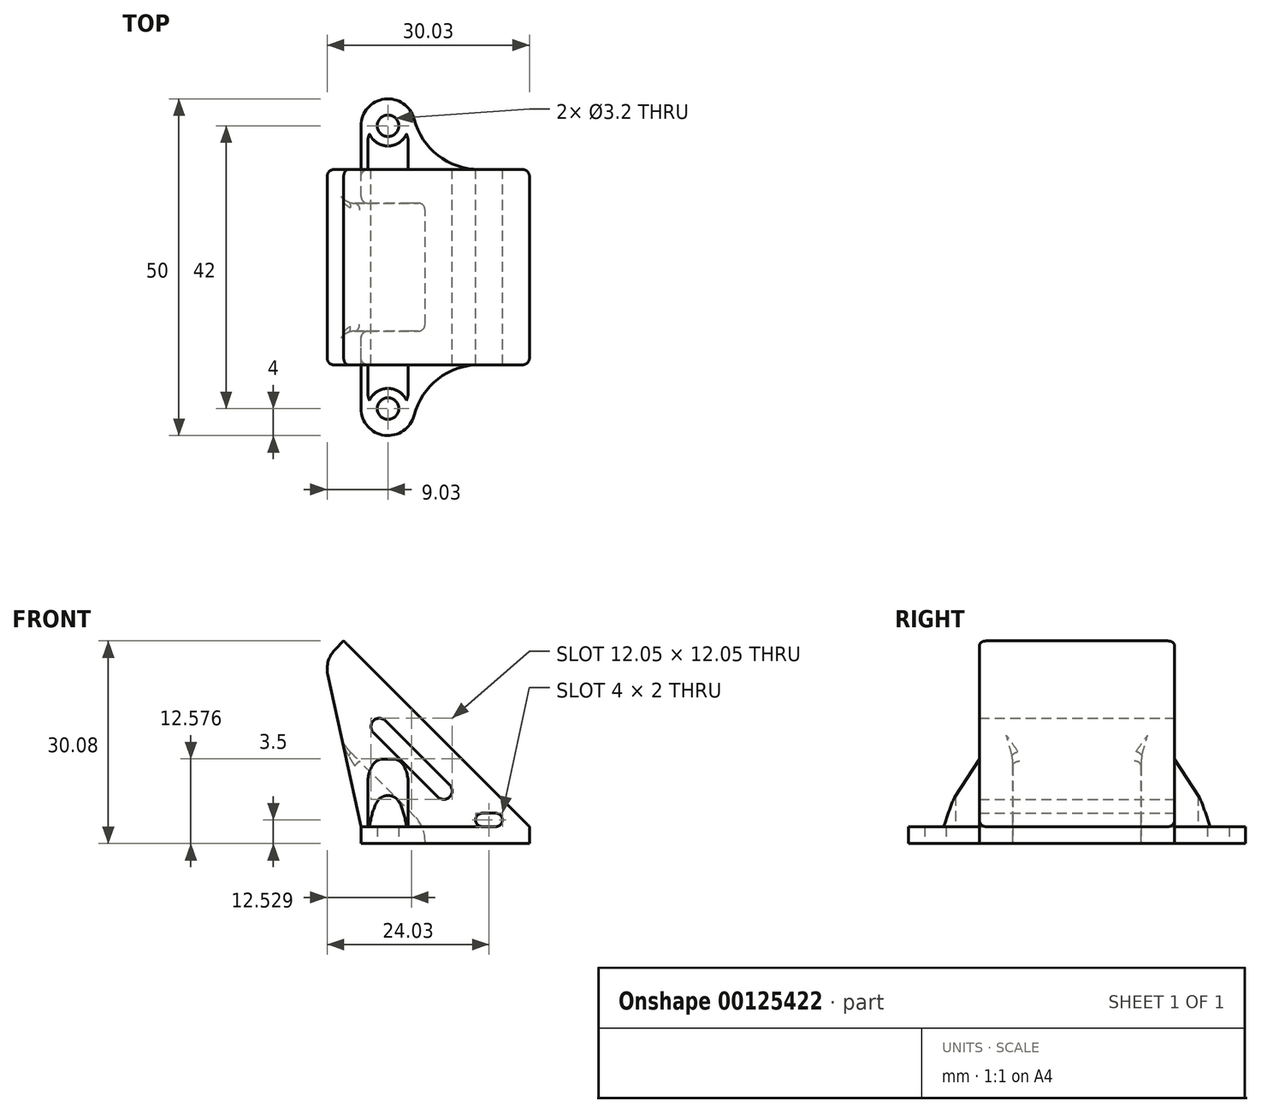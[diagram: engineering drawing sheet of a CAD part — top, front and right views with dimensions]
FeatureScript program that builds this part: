
annotation { "Feature Type Name" : "Feature", "Feature Type Description" : "" }
export const myFeature = defineFeature(function(context is Context, id is Id, definition is map)
    precondition{}
    {
        {
            var Q0;
            Q0=qCreatedBy(makeId("Front.planeOp"),FACE);
            var sketch = newSketch(context, id + "F0", { "sketchPlane" : qUnion([Q0])});
            skLineSegment(sketch, "E0", {"start": v(-27.58, 30.08) * mm, "end": v(0, 2.5) * mm});
            skLineSegment(sketch, "E1", {"start": v(-27.58, 30.08) * mm, "end": v(-28.86, 28.8) * mm});
            skLineSegment(sketch, "E2", {"start": v(-29.94, 25.11) * mm, "end": v(-25, 2.5) * mm});
            skLineSegment(sketch, "E3", {"start": v(0, 0) * mm, "end": v(0, 2.5) * mm});
            skLineSegment(sketch, "E4", {"start": v(-23.16, 18.23) * mm, "end": v(-23.16, 18.23) * mm});
            skLineSegment(sketch, "E5", {"start": v(-23.16, 16.47) * mm, "end": v(-13.61, 6.92) * mm});
            skLineSegment(sketch, "E6", {"start": v(-11.84, 6.92) * mm, "end": v(-11.84, 6.92) * mm});
            skLineSegment(sketch, "E7", {"start": v(-11.84, 8.69) * mm, "end": v(-21.39, 18.23) * mm});
            skLineSegment(sketch, "E8", {"start": v(-13.79, 16.29) * mm, "end": v(-16.62, 13.46) * mm, "construction": true});
            skPoint(sketch, "E9.visualSharp", {"position": v(-22.27, 19.12) * mm});
            skArc(sketch, "E9.filletArc", {"start": v(-21.39, 18.23) * mm, "mid": v(-22.27, 18.6) * mm, "end": v(-23.16, 18.23) * mm});
            skPoint(sketch, "E10.visualSharp", {"position": v(-10.96, 7.8) * mm});
            skArc(sketch, "E10.filletArc", {"start": v(-11.84, 6.92) * mm, "mid": v(-11.48, 7.8) * mm, "end": v(-11.84, 8.69) * mm});
            skPoint(sketch, "E11.visualSharp", {"position": v(-12.73, 6.04) * mm});
            skArc(sketch, "E11.filletArc", {"start": v(-13.61, 6.92) * mm, "mid": v(-12.73, 6.55) * mm, "end": v(-11.84, 6.92) * mm});
            skPoint(sketch, "E12.visualSharp", {"position": v(-24.04, 17.35) * mm});
            skArc(sketch, "E12.filletArc", {"start": v(-23.16, 18.23) * mm, "mid": v(-23.52, 17.35) * mm, "end": v(-23.16, 16.47) * mm});
            skLineSegment(sketch, "E13", {"start": v(-7, 3.5) * mm, "end": v(-5, 3.5) * mm, "construction": true});
            skArc(sketch, "E14.0.startCap", {"start": v(-7, 2.5) * mm, "mid": v(-8, 3.5) * mm, "end": v(-7, 4.5) * mm});
            skArc(sketch, "E14.0.endCap", {"start": v(-5, 4.5) * mm, "mid": v(-4, 3.5) * mm, "end": v(-5, 2.5) * mm});
            skLineSegment(sketch, "E14.0.left", {"start": v(-7, 4.5) * mm, "end": v(-5, 4.5) * mm});
            skLineSegment(sketch, "E14.0.right", {"start": v(-7, 2.5) * mm, "end": v(-5, 2.5) * mm});
            skPoint(sketch, "E15.visualSharp", {"position": v(-30.4, 27.25) * mm});
            skArc(sketch, "E15.filletArc", {"start": v(-28.86, 28.8) * mm, "mid": v(-29.87, 27.1) * mm, "end": v(-29.94, 25.11) * mm});
            skLineSegment(sketch, "E16", {"start": v(0, 0) * mm, "end": v(-25, 0) * mm});
            skLineSegment(sketch, "E17", {"start": v(-25, 2.5) * mm, "end": v(-25, 0) * mm});
            skSolve(sketch);
        }
        {
            var Q0;
            Q0=makeQuery(id+"F0.imprint","IMPRINT",FACE,{"disambiguationData":[TD([[makeQuery(id+"F0.imprint","IMPRINT",EDGE,{"derivedFrom":sQuery(id+"F0.wireOp",EDGE,"E0")}),-1.0]])]});
            extrude(context, id + "F1", {"entities" : qUnion([Q0]), "endBound" : BoundingType.SYMMETRIC, "depth" : 29 * mm, "offsetDistance" : 25 * mm});
        }
        {
            var Q0;
            Q0=makeQuery(id+"F1.opExtrude","SWEPT_FACE",FACE,{"disambiguationData":[OSD([sQuery(id+"F0.wireOp",EDGE,"E16")])]});
            var sketch = newSketch(context, id + "F2", { "sketchPlane" : qUnion([Q0])});
            skCircle(sketch, "E18", {"center": v(-21, 21) * mm, "radius": 1.6 * mm});
            skArc(sketch, "E19", {"start": v(-17.13, 22) * mm, "mid": v(-21.5, 24.97) * mm, "end": v(-25, 21) * mm});
            skCircle(sketch, "E20.MirrorC", {"center": v(-21, -21) * mm, "radius": 1.6 * mm});
            skLineSegment(sketch, "E21", {"start": v(-25, 21) * mm, "end": v(-25, -21) * mm});
            skArc(sketch, "E22", {"start": v(-17.13, 22) * mm, "mid": v(-13.57, 16.6) * mm, "end": v(-7.44, 14.5) * mm});
            skLineSegment(sketch, "E23", {"start": v(-7.44, 14.5) * mm, "end": v(-7.44, -14.5) * mm});
            skArc(sketch, "E24.MirrorCS", {"start": v(-17.13, -22) * mm, "mid": v(-21.5, -24.97) * mm, "end": v(-25, -21) * mm});
            skArc(sketch, "E25.MirrorCS", {"start": v(-17.13, -22) * mm, "mid": v(-13.57, -16.6) * mm, "end": v(-7.44, -14.5) * mm});
            skSolve(sketch);
        }
        {
            var Q0;
            Q0=qSketchRegion(id+"F2",true);
            extrude(context, id + "F3", {"entities" : qUnion([Q0]), "operationType" : NewBodyOperationType.ADD, "oppositeDirection" : true, "depth" : 2.5 * mm, "offsetDistance" : 25 * mm});
        }
        {
            var Q0;
            Q0=makeQuery(id+"F1.opExtrude","CAP_EDGE",EDGE,{"disambiguationData":[OSD([sQuery(id+"F0.wireOp",EDGE,"E3")])],"isStart":false});
            var Q1;
            Q1=makeQuery(id+"F1.opExtrude","CAP_EDGE",EDGE,{"disambiguationData":[OSD([sQuery(id+"F0.wireOp",EDGE,"E3")])],"isStart":true});
            var Q2;
            Q2=makeQuery(id+"F1.opExtrude","CAP_EDGE",EDGE,{"disambiguationData":[OSD([sQuery(id+"F0.wireOp",EDGE,"E1")])],"isStart":false});
            var Q3;
            Q3=makeQuery(id+"F1.opExtrude","CAP_EDGE",EDGE,{"disambiguationData":[OSD([sQuery(id+"F0.wireOp",EDGE,"E1")])],"isStart":true});
            fillet(context, id + "F4", {"entities" : qUnion([Q0, Q1, Q2, Q3]), "radius" : 1 * mm, "tangentPropagation" : true, "allowEdgeOverflow" : false});
        }
        {
            var Q0;
            Q0=qCreatedBy(makeId("Front.planeOp"),FACE);
            var sketch = newSketch(context, id + "F5", { "sketchPlane" : qUnion([Q0])});
            skLineSegment(sketch, "E26", {"start": v(-15.5, 0) * mm, "end": v(-15.5, 2.5) * mm});
            skLineSegment(sketch, "E27", {"start": v(-15.5, 2.5) * mm, "end": v(-35.5, 22.5) * mm});
            skLineSegment(sketch, "E28", {"start": v(-35.5, 22.5) * mm, "end": v(-35.5, 0) * mm});
            skLineSegment(sketch, "E29", {"start": v(-35.5, 0) * mm, "end": v(-15.5, 0) * mm});
            skSolve(sketch);
        }
        {
            var Q0;
            Q0=makeQuery(id+"F5.imprint","IMPRINT",FACE,{"disambiguationData":[TD([[makeQuery(id+"F5.imprint","IMPRINT",EDGE,{"derivedFrom":sQuery(id+"F5.wireOp",EDGE,"E26")}),1.0]])]});
            extrude(context, id + "F6", {"entities" : qUnion([Q0]), "operationType" : NewBodyOperationType.REMOVE, "endBound" : BoundingType.SYMMETRIC, "depth" : 19 * mm, "offsetDistance" : 25 * mm});
        }
        {
            var Q0;
            Q0=makeQuery(id+"F6.boolean.opBoolean","INTERSECT",EDGE,{"derivedFrom":[makeQuery(id+"F1.opExtrude","SWEPT_FACE",FACE,{"disambiguationData":[OSD([sQuery(id+"F0.wireOp",EDGE,"E2")])]}),makeQuery(id+"F6.opExtrude","SWEPT_FACE",FACE,{"disambiguationData":[OSD([sQuery(id+"F5.wireOp",EDGE,"E27")])]})]});
            var Q1;
            Q1=makeQuery(id+"F6.boolean.opBoolean","COPY",EDGE,{"derivedFrom":makeQuery(id+"F6.opExtrude","SWEPT_EDGE",EDGE,{"disambiguationData":[OSD([sQuery(id+"F5.wireOp",EDGE,"E26"),sQuery(id+"F5.wireOp",EDGE,"E27")])]})});
            fillet(context, id + "F7", {"entities" : qUnion([Q0, Q1]), "radius" : 5 * mm, "tangentPropagation" : true, "allowEdgeOverflow" : false});
        }
        {
            var Q0;
            Q0=makeQuery(id+"F6.boolean.opBoolean","INTERSECT",EDGE,{"derivedFrom":[makeQuery(id+"F1.opExtrude","SWEPT_FACE",FACE,{"disambiguationData":[OSD([sQuery(id+"F0.wireOp",EDGE,"E2")])]}),makeQuery(id+"F6.opExtrude","CAP_FACE",FACE,{"disambiguationData":[OSD([sQuery(id+"F5.wireOp",EDGE,"E26"),sQuery(id+"F5.wireOp",EDGE,"E27"),sQuery(id+"F5.wireOp",EDGE,"E28"),sQuery(id+"F5.wireOp",EDGE,"E29")])],"isStart":true})]});
            var Q1;
            Q1=makeQuery(id+"F6.boolean.opBoolean","INTERSECT",EDGE,{"derivedFrom":[makeQuery(id+"F1.opExtrude","SWEPT_FACE",FACE,{"disambiguationData":[OSD([sQuery(id+"F0.wireOp",EDGE,"E2")])]}),makeQuery(id+"F6.opExtrude","CAP_FACE",FACE,{"disambiguationData":[OSD([sQuery(id+"F5.wireOp",EDGE,"E26"),sQuery(id+"F5.wireOp",EDGE,"E27"),sQuery(id+"F5.wireOp",EDGE,"E28"),sQuery(id+"F5.wireOp",EDGE,"E29")])],"isStart":false})]});
            var Q2;
            Q2=makeQuery(id+"F6.boolean.opBoolean","INTERSECT",EDGE,{"derivedFrom":[makeQuery(id+"F3.boolean.opBoolean","MERGE",FACE,{"derivedFrom":[makeQuery(id+"F1.opExtrude","SWEPT_FACE",FACE,{"disambiguationData":[OSD([sQuery(id+"F0.wireOp",EDGE,"E17")])]}),makeQuery(id+"F3.opExtrude","SWEPT_FACE",FACE,{"disambiguationData":[OSD([sQuery(id+"F2.wireOp",EDGE,"E21")])]})]}),makeQuery(id+"F6.opExtrude","CAP_FACE",FACE,{"disambiguationData":[OSD([sQuery(id+"F5.wireOp",EDGE,"E26"),sQuery(id+"F5.wireOp",EDGE,"E27"),sQuery(id+"F5.wireOp",EDGE,"E28"),sQuery(id+"F5.wireOp",EDGE,"E29")])],"isStart":true})]});
            var Q3;
            Q3=makeQuery(id+"F6.boolean.opBoolean","INTERSECT",EDGE,{"derivedFrom":[makeQuery(id+"F3.boolean.opBoolean","MERGE",FACE,{"derivedFrom":[makeQuery(id+"F1.opExtrude","SWEPT_FACE",FACE,{"disambiguationData":[OSD([sQuery(id+"F0.wireOp",EDGE,"E17")])]}),makeQuery(id+"F3.opExtrude","SWEPT_FACE",FACE,{"disambiguationData":[OSD([sQuery(id+"F2.wireOp",EDGE,"E21")])]})]}),makeQuery(id+"F6.opExtrude","CAP_FACE",FACE,{"disambiguationData":[OSD([sQuery(id+"F5.wireOp",EDGE,"E26"),sQuery(id+"F5.wireOp",EDGE,"E27"),sQuery(id+"F5.wireOp",EDGE,"E28"),sQuery(id+"F5.wireOp",EDGE,"E29")])],"isStart":false})]});
            fillet(context, id + "F8", {"entities" : qUnion([Q0, Q1, Q2, Q3]), "radius" : 1 * mm, "tangentPropagation" : true, "allowEdgeOverflow" : false});
        }
        {
            var Q0;
            Q0=makeQuery(id+"F6.boolean.opBoolean","COPY",FACE,{"derivedFrom":makeQuery(id+"F6.opExtrude","SWEPT_FACE",FACE,{"disambiguationData":[OSD([sQuery(id+"F5.wireOp",EDGE,"E27")])]})});
            fillet(context, id + "F9", {"entities" : qUnion([Q0]), "radius" : 1 * mm, "tangentPropagation" : true, "allowEdgeOverflow" : false});
        }
        {
            var Q0;
            {var subQ4=sQuery(id+"F2.wireOp",EDGE,"E21");var subQ6=sQuery(id+"F2.wireOp",EDGE,"E19");Q0=makeQuery(id+"F6.boolean.opBoolean","SPLIT",FACE,{"disambiguationData":[TD([makeQuery(id+"F3.opExtrude","SWEPT_FACE",FACE,{"disambiguationData":[OSD([subQ6])]})])],"derivedFrom":makeQuery(id+"F3.boolean.opBoolean","MERGE",FACE,{"derivedFrom":[makeQuery(id+"F1.opExtrude","SWEPT_FACE",FACE,{"disambiguationData":[OSD([sQuery(id+"F0.wireOp",EDGE,"E17")])]}),makeQuery(id+"F3.opExtrude","SWEPT_FACE",FACE,{"disambiguationData":[OSD([subQ4])]})]})});}
            var sketch = newSketch(context, id + "F10", { "sketchPlane" : qUnion([Q0])});
            skLineSegment(sketch, "E30", {"start": v(-21, 2.5) * mm, "end": v(-14.5, 12.5) * mm});
            skLineSegment(sketch, "E31", {"start": v(-14.5, 12.5) * mm, "end": v(-14.5, 2.5) * mm});
            skLineSegment(sketch, "E32", {"start": v(-14.5, 2.5) * mm, "end": v(-21, 2.5) * mm});
            skSolve(sketch);
        }
        {
            var Q0;
            Q0=makeQuery(id+"F10.imprint","IMPRINT",FACE,{"disambiguationData":[TD([[makeQuery(id+"F10.imprint","IMPRINT",EDGE,{"derivedFrom":sQuery(id+"F10.wireOp",EDGE,"E30")}),-1.0]])]});
            extrude(context, id + "F11", {"entities" : qUnion([Q0]), "oppositeDirection" : true, "depth" : 7 * mm, "offsetDistance" : 25 * mm, "hasSecondDirection" : true, "secondDirectionOppositeDirection" : true, "secondDirectionDepth" : 1 * mm});
        }
        {
            var Q0;
            Q0=makeQuery(id+"F11.opExtrude","SWEPT_BODY",BODY,{"disambiguationData":[OSD([sQuery(id+"F10.wireOp",EDGE,"E30"),sQuery(id+"F10.wireOp",EDGE,"E31"),sQuery(id+"F10.wireOp",EDGE,"E32")])]});
            var Q1;
            Q1=qCreatedBy(makeId("Front.planeOp"),FACE);
            mirror(context, id + "F12", {"operationType" : NewBodyOperationType.ADD, "entities" : qUnion([Q0]), "mirrorPlane" : qUnion([Q1])});
        }
        {
            var Q0;
            {var subQ0=sQuery(id+"F2.wireOp",EDGE,"E20.MirrorC");var subQ2=sQuery(id+"F2.wireOp",EDGE,"E21");var subQ4=sQuery(id+"F2.wireOp",EDGE,"E24.MirrorCS");var subQ5=sQuery(id+"F2.wireOp",EDGE,"E25.MirrorCS");Q0=makeQuery(id+"F3.boolean.opBoolean","SPLIT",FACE,{"disambiguationData":[TD([makeQuery(id+"F3.opExtrude","SWEPT_FACE",FACE,{"disambiguationData":[OSD([subQ0])]})])],"derivedFrom":makeQuery(id+"F3.opExtrude","CAP_FACE",FACE,{"disambiguationData":[OSD([sQuery(id+"F2.wireOp",EDGE,"E18"),sQuery(id+"F2.wireOp",EDGE,"E19"),subQ0,subQ2,sQuery(id+"F2.wireOp",EDGE,"E22"),sQuery(id+"F2.wireOp",EDGE,"E23"),subQ4,subQ5])],"isStart":false})});}
            var sketch = newSketch(context, id + "F13", { "sketchPlane" : qUnion([Q0])});
            skCircle(sketch, "E33", {"center": v(-21, 21) * mm, "radius": 3 * mm});
            skCircle(sketch, "E34", {"center": v(-21, -21) * mm, "radius": 3 * mm});
            skSolve(sketch);
        }
        {
            var Q0;
            Q0=makeQuery(id+"F11.opExtrude","CAP_EDGE",EDGE,{"disambiguationData":[OSD([sQuery(id+"F10.wireOp",EDGE,"E30")])],"isStart":true});
            var Q1;
            Q1=makeQuery(id+"F11.opExtrude","CAP_EDGE",EDGE,{"disambiguationData":[OSD([sQuery(id+"F10.wireOp",EDGE,"E30")])],"isStart":false});
            var Q2;
            Q2=makeQuery(id+"F12.opPattern","COPY",EDGE,{"derivedFrom":makeQuery(id+"F11.opExtrude","CAP_EDGE",EDGE,{"disambiguationData":[OSD([sQuery(id+"F10.wireOp",EDGE,"E30")])],"isStart":true}),"instanceName":"1"});
            var Q3;
            Q3=makeQuery(id+"F12.opPattern","COPY",EDGE,{"derivedFrom":makeQuery(id+"F11.opExtrude","CAP_EDGE",EDGE,{"disambiguationData":[OSD([sQuery(id+"F10.wireOp",EDGE,"E30")])],"isStart":false}),"instanceName":"1"});
            fillet(context, id + "F14", {"entities" : qUnion([Q0, Q1, Q2, Q3]), "radius" : 2 * mm, "tangentPropagation" : true, "allowEdgeOverflow" : false});
        }
        {
            var Q0;
            Q0=qSketchRegion(id+"F13",true);
            extrude(context, id + "F15", {"entities" : qUnion([Q0]), "operationType" : NewBodyOperationType.REMOVE, "depth" : 25 * mm, "offsetDistance" : 25 * mm});
        }
    });
